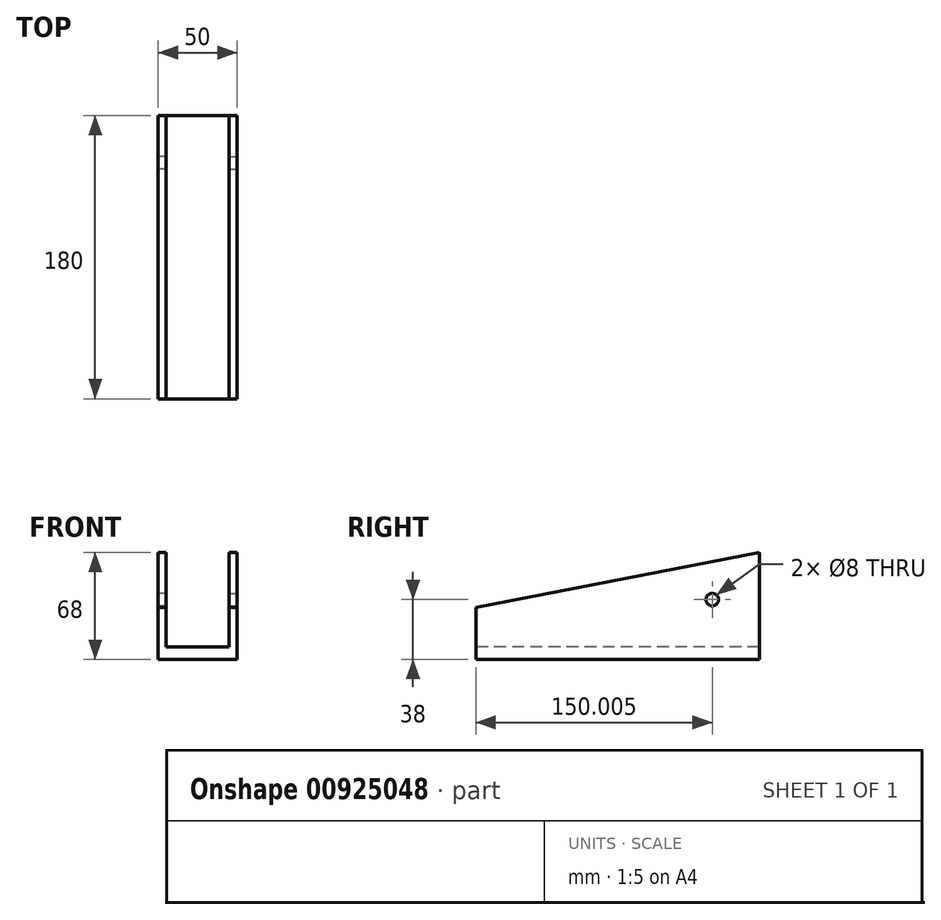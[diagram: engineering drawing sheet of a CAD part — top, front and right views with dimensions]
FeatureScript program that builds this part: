
annotation { "Feature Type Name" : "Feature", "Feature Type Description" : "" }
export const myFeature = defineFeature(function(context is Context, id is Id, definition is map)
    precondition{}
    {
        {
            var Q0;
            Q0=qCreatedBy(makeId("Top.planeOp"),FACE);
            var sketch = newSketch(context, id + "F0", { "sketchPlane" : qUnion([Q0])});
            skLineSegment(sketch, "E0.bottom", {"start": v(-27.45, 74.86) * mm, "end": v(22.55, 74.86) * mm});
            skLineSegment(sketch, "E0.top", {"start": v(-27.45, -105.14) * mm, "end": v(22.55, -105.14) * mm});
            skLineSegment(sketch, "E0.left", {"start": v(-27.45, 74.86) * mm, "end": v(-27.45, -105.14) * mm});
            skLineSegment(sketch, "E0.right", {"start": v(22.55, 74.86) * mm, "end": v(22.55, -105.14) * mm});
            skSolve(sketch);
        }
        {
            var Q0;
            Q0=makeQuery(id+"F0.imprint","IMPRINT",FACE,{"disambiguationData":[TD([[makeQuery(id+"F0.imprint","IMPRINT",EDGE,{"derivedFrom":sQuery(id+"F0.wireOp",EDGE,"E0.bottom")}),-1.0]])]});
            extrude(context, id + "F1", {"entities" : qUnion([Q0]), "oppositeDirection" : true, "depth" : 8 * mm, "offsetDistance" : 25 * mm});
        }
        {
            var Q0;
            Q0=makeQuery(id+"F1.opExtrude","SWEPT_FACE",FACE,{"disambiguationData":[OSD([sQuery(id+"F0.wireOp",EDGE,"E0.left")])]});
            var sketch = newSketch(context, id + "F2", { "sketchPlane" : qUnion([Q0])});
            skLineSegment(sketch, "E1", {"start": v(-74.86, 0) * mm, "end": v(-74.86, 60) * mm});
            skLineSegment(sketch, "E2", {"start": v(105.14, 0) * mm, "end": v(105.14, 25) * mm});
            skLineSegment(sketch, "E3", {"start": v(105.14, 25) * mm, "end": v(-74.86, 60) * mm});
            skLineSegment(sketch, "E4", {"start": v(-74.86, 0) * mm, "end": v(105.14, 0) * mm});
            skCircle(sketch, "E5", {"center": v(-44.86, 30) * mm, "radius": 4 * mm});
            skSolve(sketch);
        }
        {
            var Q0;
            Q0=makeQuery(id+"F2.imprint","IMPRINT",FACE,{"disambiguationData":[TD([[makeQuery(id+"F2.imprint","IMPRINT",EDGE,{"derivedFrom":sQuery(id+"F2.wireOp",EDGE,"E1")}),-1.0]])]});
            extrude(context, id + "F3", {"entities" : qUnion([Q0]), "operationType" : NewBodyOperationType.ADD, "oppositeDirection" : true, "depth" : 5 * mm, "offsetDistance" : 25 * mm});
        }
        {
            var Q0;
            Q0=makeQuery(id+"F1.opExtrude","SWEPT_FACE",FACE,{"disambiguationData":[OSD([sQuery(id+"F0.wireOp",EDGE,"E0.right")])]});
            var sketch = newSketch(context, id + "F4", { "sketchPlane" : qUnion([Q0])});
            skLineSegment(sketch, "E6", {"start": v(-105.14, 0) * mm, "end": v(-105.14, 25) * mm});
            skLineSegment(sketch, "E7", {"start": v(-105.14, 25) * mm, "end": v(74.86, 60) * mm});
            skLineSegment(sketch, "E8", {"start": v(74.86, 60) * mm, "end": v(74.86, 0) * mm});
            skLineSegment(sketch, "E9", {"start": v(74.86, 0) * mm, "end": v(-105.14, 0) * mm});
            skCircle(sketch, "E10", {"center": v(44.86, 30) * mm, "radius": 4 * mm});
            skSolve(sketch);
        }
        {
            var Q0;
            Q0 = qSketchRegion(id + "F4", true);
            extrude(context, id + "F5", {"entities" : qUnion([Q0]), "operationType" : NewBodyOperationType.ADD, "oppositeDirection" : true, "depth" : 5 * mm, "offsetDistance" : 25 * mm});
        }
    });
